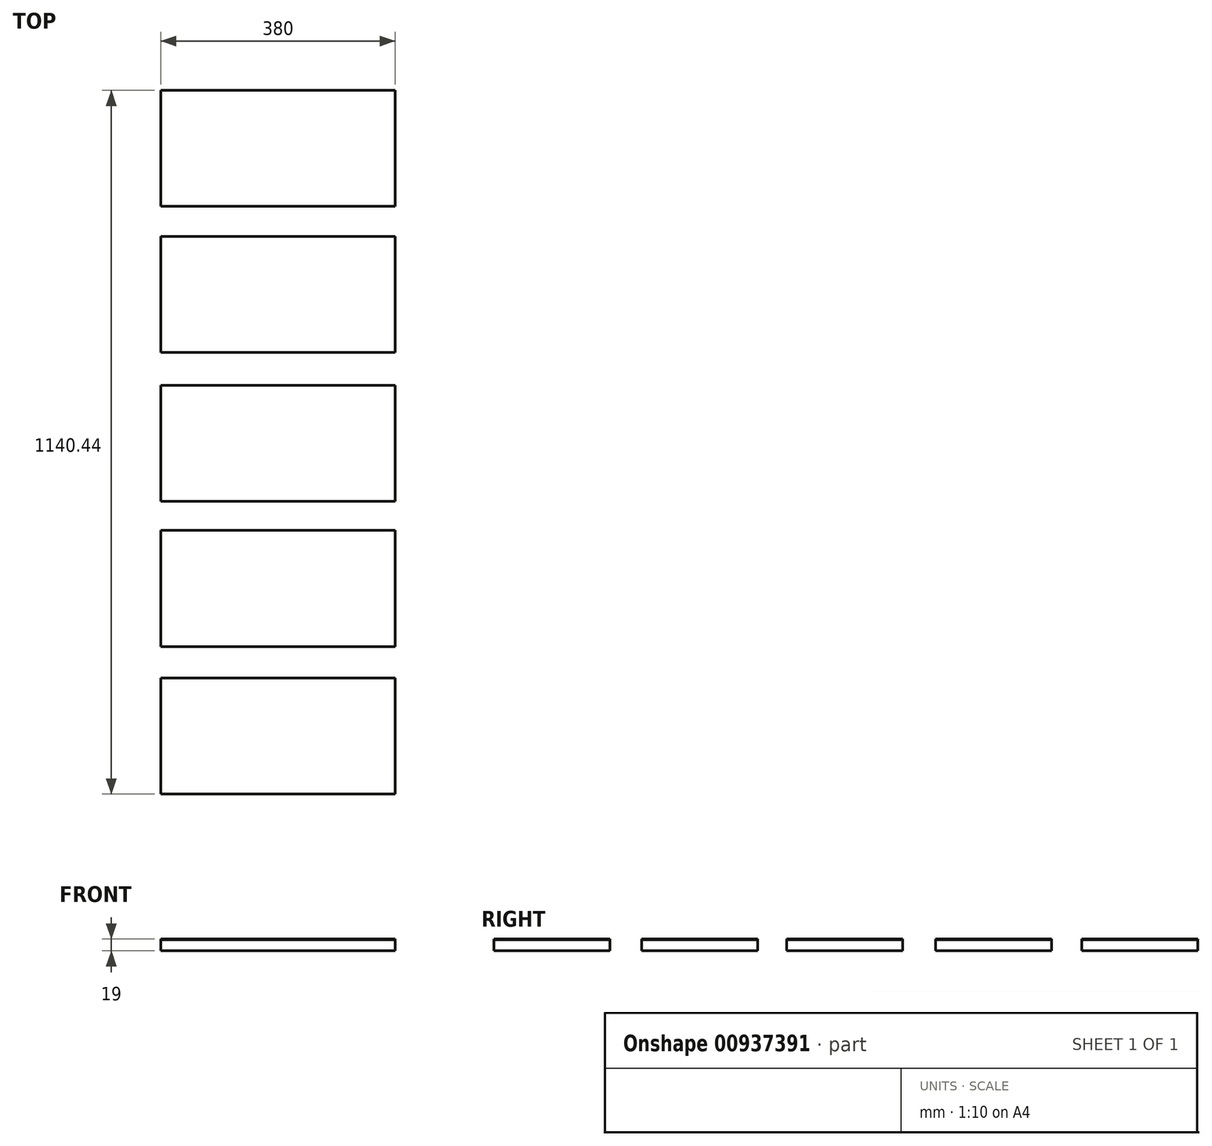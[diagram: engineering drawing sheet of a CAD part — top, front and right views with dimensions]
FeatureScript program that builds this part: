
annotation { "Feature Type Name" : "Feature", "Feature Type Description" : "" }
export const myFeature = defineFeature(function(context is Context, id is Id, definition is map)
    precondition{}
    {
        {
            var Q0;
            Q0=qCreatedBy(makeId("Top.planeOp"),FACE);
            var sketch = newSketch(context, id + "F0", { "sketchPlane" : qUnion([Q0])});
            skLineSegment(sketch, "E0.bottom", {"start": v(-305, -610) * mm, "end": v(305, -610) * mm, "construction": true});
            skLineSegment(sketch, "E0.top", {"start": v(-305, 610) * mm, "end": v(305, 610) * mm, "construction": true});
            skLineSegment(sketch, "E0.left", {"start": v(-305, -610) * mm, "end": v(-305, 610) * mm, "construction": true});
            skLineSegment(sketch, "E0.right", {"start": v(305, -610) * mm, "end": v(305, 610) * mm, "construction": true});
            skPoint(sketch, "E0.middle", {"position": v(0, 0) * mm});
            skLineSegment(sketch, "E1.bottom", {"start": v(-250.56, 577.85) * mm, "end": v(129.44, 577.85) * mm});
            skLineSegment(sketch, "E1.top", {"start": v(-250.56, 389.85) * mm, "end": v(129.44, 389.85) * mm});
            skLineSegment(sketch, "E1.left", {"start": v(-250.56, 577.85) * mm, "end": v(-250.56, 389.85) * mm});
            skLineSegment(sketch, "E1.right", {"start": v(129.44, 577.85) * mm, "end": v(129.44, 389.85) * mm});
            skLineSegment(sketch, "E2.bottom", {"start": v(-250.56, 341.16) * mm, "end": v(129.44, 341.16) * mm});
            skLineSegment(sketch, "E2.top", {"start": v(-250.56, 153.16) * mm, "end": v(129.44, 153.16) * mm});
            skLineSegment(sketch, "E2.left", {"start": v(-250.56, 341.16) * mm, "end": v(-250.56, 153.16) * mm});
            skLineSegment(sketch, "E2.right", {"start": v(129.44, 341.16) * mm, "end": v(129.44, 153.16) * mm});
            skLineSegment(sketch, "E3.bottom", {"start": v(-250.56, 99.78) * mm, "end": v(129.44, 99.78) * mm});
            skLineSegment(sketch, "E3.top", {"start": v(-250.56, -88.22) * mm, "end": v(129.44, -88.22) * mm});
            skLineSegment(sketch, "E3.left", {"start": v(-250.56, 99.78) * mm, "end": v(-250.56, -88.22) * mm});
            skLineSegment(sketch, "E3.right", {"start": v(129.44, 99.78) * mm, "end": v(129.44, -88.22) * mm});
            skLineSegment(sketch, "E4.bottom", {"start": v(-250.56, -135.3) * mm, "end": v(129.44, -135.3) * mm});
            skLineSegment(sketch, "E4.top", {"start": v(-250.56, -323.3) * mm, "end": v(129.44, -323.3) * mm});
            skLineSegment(sketch, "E4.left", {"start": v(-250.56, -135.3) * mm, "end": v(-250.56, -323.3) * mm});
            skLineSegment(sketch, "E4.right", {"start": v(129.44, -135.3) * mm, "end": v(129.44, -323.3) * mm});
            skLineSegment(sketch, "E5.bottom", {"start": v(-250.56, -374.59) * mm, "end": v(129.44, -374.59) * mm});
            skLineSegment(sketch, "E5.top", {"start": v(-250.56, -562.59) * mm, "end": v(129.44, -562.59) * mm});
            skLineSegment(sketch, "E5.left", {"start": v(-250.56, -374.59) * mm, "end": v(-250.56, -562.59) * mm});
            skLineSegment(sketch, "E5.right", {"start": v(129.44, -374.59) * mm, "end": v(129.44, -562.59) * mm});
            skSolve(sketch);
        }
        {
            var Q0;
            Q0=makeQuery(id+"F0.imprint","IMPRINT",FACE,{"disambiguationData":[TD([[makeQuery(id+"F0.imprint","IMPRINT",EDGE,{"derivedFrom":sQuery(id+"F0.wireOp",EDGE,"E2.bottom")}),-1.0]])]});
            var Q1;
            Q1=makeQuery(id+"F0.imprint","IMPRINT",FACE,{"disambiguationData":[TD([[makeQuery(id+"F0.imprint","IMPRINT",EDGE,{"derivedFrom":sQuery(id+"F0.wireOp",EDGE,"E1.bottom")}),-1.0]])]});
            var Q2;
            Q2=makeQuery(id+"F0.imprint","IMPRINT",FACE,{"disambiguationData":[TD([[makeQuery(id+"F0.imprint","IMPRINT",EDGE,{"derivedFrom":sQuery(id+"F0.wireOp",EDGE,"E3.bottom")}),-1.0]])]});
            var Q3;
            Q3=makeQuery(id+"F0.imprint","IMPRINT",FACE,{"disambiguationData":[TD([[makeQuery(id+"F0.imprint","IMPRINT",EDGE,{"derivedFrom":sQuery(id+"F0.wireOp",EDGE,"E4.bottom")}),-1.0]])]});
            var Q4;
            Q4=makeQuery(id+"F0.imprint","IMPRINT",FACE,{"disambiguationData":[TD([[makeQuery(id+"F0.imprint","IMPRINT",EDGE,{"derivedFrom":sQuery(id+"F0.wireOp",EDGE,"E5.bottom")}),-1.0]])]});
            var Q5;
            Q5=sQuery(id+"F0.wireOp",EDGE,"E0.left");
            var Q6;
            Q6=sQuery(id+"F0.wireOp",EDGE,"E0.top");
            var Q7;
            Q7=sQuery(id+"F0.wireOp",EDGE,"E0.right");
            var Q8;
            Q8=sQuery(id+"F0.wireOp",EDGE,"E0.bottom");
            extrude(context, id + "F1", {"entities" : qUnion([Q0, Q1, Q2, Q3, Q4]), "surfaceEntities" : qUnion([Q5, Q6, Q7, Q8]), "depth" : 19 * mm, "offsetDistance" : 25 * mm});
        }
        {
            var Q0;
            Q0 = qSketchRegion(id + "F0", true);
            extrude(context, id + "F2", {"entities" : qUnion([Q0]), "depth" : 18 * mm, "offsetDistance" : 25 * mm});
        }
    });
